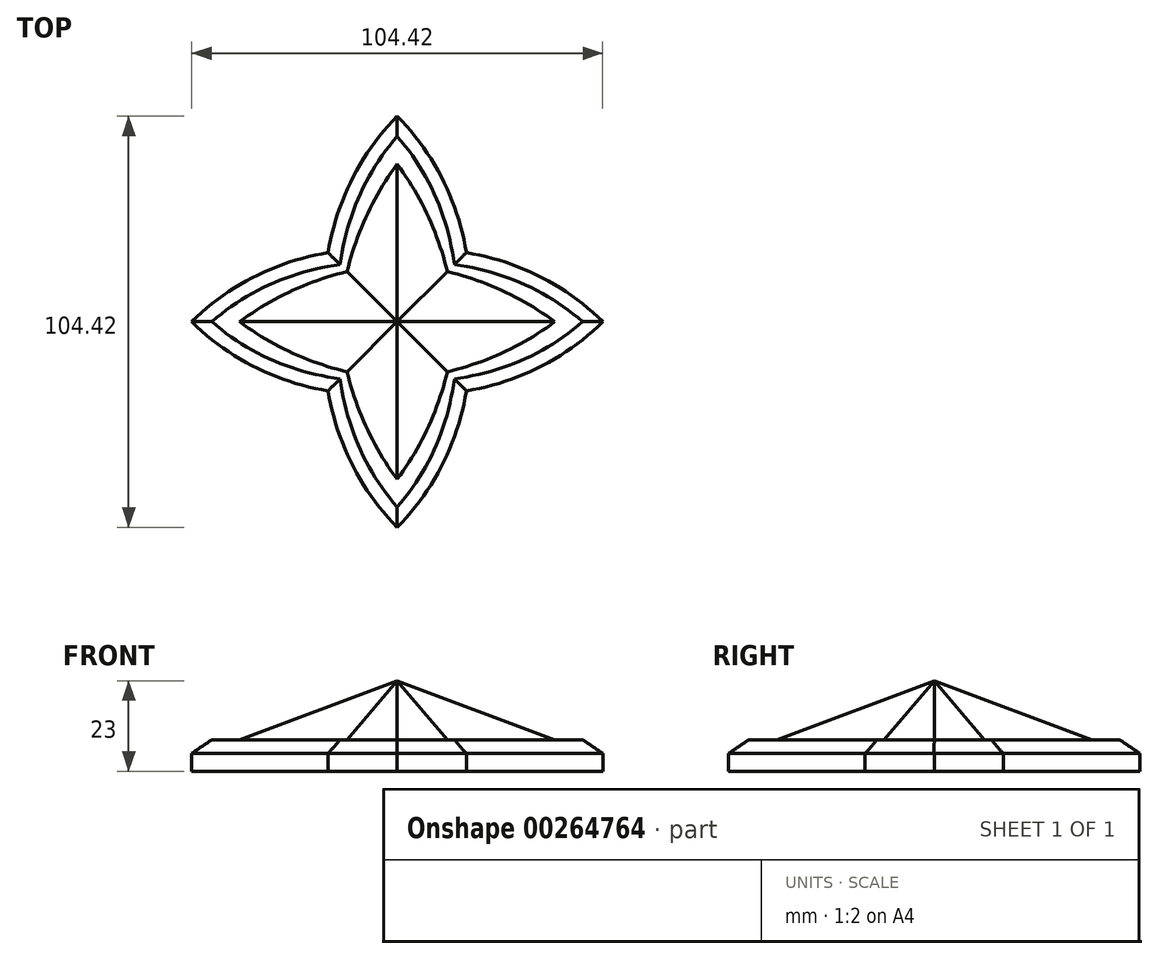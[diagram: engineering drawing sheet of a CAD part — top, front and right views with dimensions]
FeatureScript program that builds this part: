
annotation { "Feature Type Name" : "Feature", "Feature Type Description" : "" }
export const myFeature = defineFeature(function(context is Context, id is Id, definition is map)
    precondition{}
    {
        {
            var Q0;
            Q0=qCreatedBy(makeId("Top.planeOp"),FACE);
            var sketch = newSketch(context, id + "F0", { "sketchPlane" : qUnion([Q0])});
            skLineSegment(sketch, "E0", {"start": v(0, 49.48) * mm, "end": v(0, -50.52) * mm, "construction": true});
            skSolve(sketch);
        }
        {
            var Q0;
            Q0=qCreatedBy(makeId("Top.planeOp"),FACE);
            var sketch = newSketch(context, id + "F1", { "sketchPlane" : qUnion([Q0])});
            skFitSpline(sketch, "E1", {"points": [v(0, 40) * mm, v(-12.72, 12.72) * mm], "startDerivative": vector(-18.13, -24.12) * mm, "endDerivative": vector(-6.97, -29.29) * mm});
            skLineSegment(sketch, "E2", {"start": v(-12.72, 12.72) * mm, "end": v(0, 0) * mm, "construction": true});
            skFitSpline(sketch, "E3.MirrorCS", {"points": [v(-40, 0) * mm, v(-12.72, 12.72) * mm], "startDerivative": vector(24.12, 18.13) * mm, "endDerivative": vector(29.29, 6.97) * mm});
            skFitSpline(sketch, "E4.MirrorCS", {"points": [v(0, 40) * mm, v(12.72, 12.72) * mm], "startDerivative": vector(18.13, -24.12) * mm, "endDerivative": vector(6.97, -29.29) * mm});
            skFitSpline(sketch, "E5.MirrorCS", {"points": [v(40, 0) * mm, v(12.72, 12.72) * mm], "startDerivative": vector(-24.12, 18.13) * mm, "endDerivative": vector(-29.29, 6.97) * mm});
            skLineSegment(sketch, "E6", {"start": v(12.72, 12.72) * mm, "end": v(0, 0) * mm, "construction": true});
            skFitSpline(sketch, "E7.MirrorCS", {"points": [v(-40, 0) * mm, v(-12.72, -12.72) * mm], "startDerivative": vector(24.12, -18.13) * mm, "endDerivative": vector(29.29, -6.97) * mm});
            skFitSpline(sketch, "E8.MirrorCS", {"points": [v(0, -40) * mm, v(-12.72, -12.72) * mm], "startDerivative": vector(-18.13, 24.12) * mm, "endDerivative": vector(-6.97, 29.29) * mm});
            skFitSpline(sketch, "E9.MirrorCS", {"points": [v(40, 0) * mm, v(12.72, -12.72) * mm], "startDerivative": vector(-24.12, -18.13) * mm, "endDerivative": vector(-29.29, -6.97) * mm});
            skFitSpline(sketch, "E10.MirrorCS", {"points": [v(0, -40) * mm, v(12.72, -12.72) * mm], "startDerivative": vector(18.13, 24.12) * mm, "endDerivative": vector(6.97, 29.29) * mm});
            skSolve(sketch);
        }
        {
            var Q0;
            Q0=qCreatedBy(makeId("Top.planeOp"),FACE);
            cPlane(context, id + "F2", {"entities" : qUnion([Q0]), "cplaneType" : CPlaneType.OFFSET, "offset" : 15 * mm, "width" : 150 * mm, "height" : 150 * mm});
        }
        {
            var Q0;
            Q0=qCreatedBy(id+"F2.planeOp",FACE);
            var sketch = newSketch(context, id + "F3", { "sketchPlane" : qUnion([Q0])});
            skPoint(sketch, "E11", {"position": v(0, 0) * mm});
            skSolve(sketch);
        }
        {
            var Q0;
            Q0=makeQuery(id+"F1.imprint","IMPRINT",FACE,{"disambiguationData":[TD([[makeQuery(id+"F1.imprint","IMPRINT",EDGE,{"derivedFrom":sQuery(id+"F1.wireOp",EDGE,"E1")}),1.0]])]});
            var Q1;
            Q1=sQuery(id+"F3.wireOp",VERTEX,"E11");
            loft(context, id + "F4", {"sheetProfilesArray" : [{ "sheetProfileEntities" : qUnion([Q0]) }, { "sheetProfileEntities" : qUnion([Q1]) }]});
        }
        {
            var Q0;
            Q0=qCreatedBy(makeId("Top.planeOp"),FACE);
            var sketch = newSketch(context, id + "F5", { "sketchPlane" : qUnion([Q0])});
            skFitSpline(sketch, "E12", {"points": [v(0, 52.21) * mm, v(-17.56, 17.56) * mm], "startDerivative": vector(-28.05, -28.15) * mm, "endDerivative": vector(-6.22, -38.55) * mm});
            skLineSegment(sketch, "E13", {"start": v(-17.56, 17.56) * mm, "end": v(0, 0) * mm, "construction": true});
            skFitSpline(sketch, "E14.MirrorCS", {"points": [v(0, 52.21) * mm, v(17.56, 17.56) * mm], "startDerivative": vector(28.05, -28.15) * mm, "endDerivative": vector(6.22, -38.55) * mm});
            skLineSegment(sketch, "E15.MirrorCS", {"start": v(17.56, 17.56) * mm, "end": v(0, 0) * mm, "construction": true});
            skFitSpline(sketch, "E16.MirrorCS", {"points": [v(-52.21, 0) * mm, v(-17.56, 17.56) * mm], "startDerivative": vector(28.15, 28.05) * mm, "endDerivative": vector(38.55, 6.22) * mm});
            skFitSpline(sketch, "E17.MirrorCS", {"points": [v(-52.21, 0) * mm, v(-17.56, -17.56) * mm], "startDerivative": vector(28.15, -28.05) * mm, "endDerivative": vector(38.55, -6.22) * mm});
            skFitSpline(sketch, "E18.MirrorCS", {"points": [v(52.21, 0) * mm, v(17.56, 17.56) * mm], "startDerivative": vector(-28.15, 28.05) * mm, "endDerivative": vector(-38.55, 6.22) * mm});
            skFitSpline(sketch, "E19.MirrorCS", {"points": [v(52.21, 0) * mm, v(17.56, -17.56) * mm], "startDerivative": vector(-28.15, -28.05) * mm, "endDerivative": vector(-38.55, -6.22) * mm});
            skFitSpline(sketch, "E20.MirrorCS", {"points": [v(0, -52.21) * mm, v(17.56, -17.56) * mm], "startDerivative": vector(28.05, 28.15) * mm, "endDerivative": vector(6.22, 38.55) * mm});
            skFitSpline(sketch, "E21.MirrorCS", {"points": [v(0, -52.21) * mm, v(-17.56, -17.56) * mm], "startDerivative": vector(-28.05, 28.15) * mm, "endDerivative": vector(-6.22, 38.55) * mm});
            skSolve(sketch);
        }
        {
            var Q0;
            Q0=makeQuery(id+"F5.imprint","IMPRINT",FACE,{"disambiguationData":[TD([[makeQuery(id+"F5.imprint","IMPRINT",EDGE,{"derivedFrom":sQuery(id+"F5.wireOp",EDGE,"E12")}),1.0]])]});
            extrude(context, id + "F6", {"entities" : qUnion([Q0]), "operationType" : NewBodyOperationType.ADD, "oppositeDirection" : true, "depth" : 8 * mm, "offsetDistance" : 25 * mm});
        }
        {
            var Q0;
            Q0=makeQuery(id+"F6.opExtrude","CAP_EDGE",EDGE,{"disambiguationData":[OSD([sQuery(id+"F5.wireOp",EDGE,"E21.MirrorCS")])],"isStart":true});
            var Q1;
            Q1=makeQuery(id+"F6.opExtrude","CAP_EDGE",EDGE,{"disambiguationData":[OSD([sQuery(id+"F5.wireOp",EDGE,"E20.MirrorCS")])],"isStart":true});
            var Q2;
            Q2=makeQuery(id+"F6.opExtrude","CAP_EDGE",EDGE,{"disambiguationData":[OSD([sQuery(id+"F5.wireOp",EDGE,"E17.MirrorCS")])],"isStart":true});
            var Q3;
            Q3=makeQuery(id+"F6.opExtrude","CAP_EDGE",EDGE,{"disambiguationData":[OSD([sQuery(id+"F5.wireOp",EDGE,"E16.MirrorCS")])],"isStart":true});
            var Q4;
            Q4=makeQuery(id+"F6.opExtrude","CAP_EDGE",EDGE,{"disambiguationData":[OSD([sQuery(id+"F5.wireOp",EDGE,"E12")])],"isStart":true});
            var Q5;
            Q5=makeQuery(id+"F6.opExtrude","CAP_EDGE",EDGE,{"disambiguationData":[OSD([sQuery(id+"F5.wireOp",EDGE,"E14.MirrorCS")])],"isStart":true});
            var Q6;
            Q6=makeQuery(id+"F6.opExtrude","CAP_EDGE",EDGE,{"disambiguationData":[OSD([sQuery(id+"F5.wireOp",EDGE,"E18.MirrorCS")])],"isStart":true});
            var Q7;
            Q7=makeQuery(id+"F6.opExtrude","CAP_EDGE",EDGE,{"disambiguationData":[OSD([sQuery(id+"F5.wireOp",EDGE,"E19.MirrorCS")])],"isStart":true});
            chamfer(context, id + "F7", {"entities" : qUnion([Q0, Q1, Q2, Q3, Q4, Q5, Q6, Q7]), "width" : 3.5 * mm, "tangentPropagation" : true});
        }
    });
